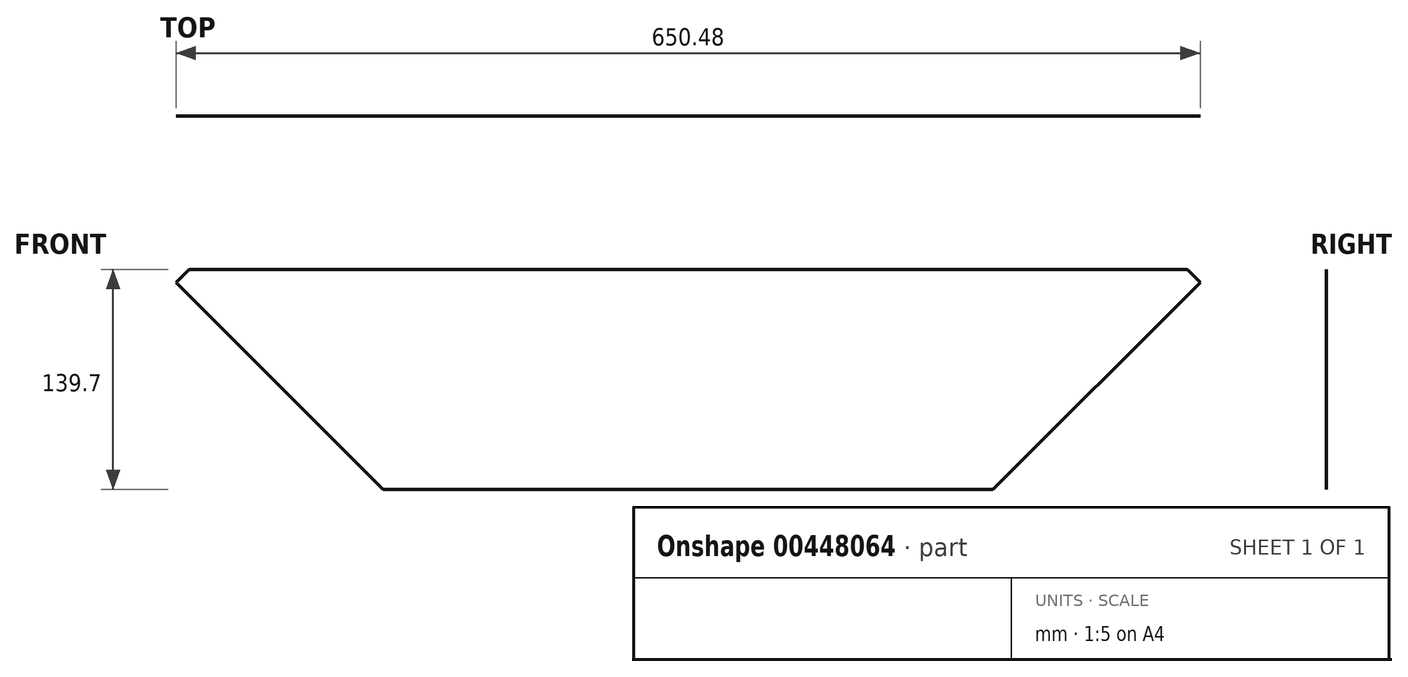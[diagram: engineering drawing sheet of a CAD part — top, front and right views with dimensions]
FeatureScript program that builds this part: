
annotation { "Feature Type Name" : "Feature", "Feature Type Description" : "" }
export const myFeature = defineFeature(function(context is Context, id is Id, definition is map)
    precondition{}
    {
        {
            var Q0;
            Q0=qCreatedBy(makeId("Front.planeOp"),FACE);
            var sketch = newSketch(context, id + "F0", { "sketchPlane" : qUnion([Q0])});
            skLineSegment(sketch, "E0", {"start": v(0, 0) * mm, "end": v(193.68, 0) * mm});
            skLineSegment(sketch, "E1", {"start": v(0, 0) * mm, "end": v(0, 139.7) * mm});
            skLineSegment(sketch, "E2", {"start": v(0, 139.7) * mm, "end": v(333.38, 139.7) * mm});
            skLineSegment(sketch, "E3", {"start": v(193.68, 0) * mm, "end": v(333.38, 139.7) * mm});
            skLineSegment(sketch, "E4.MirrorCS", {"start": v(0, 139.7) * mm, "end": v(-333.38, 139.7) * mm});
            skLineSegment(sketch, "E5.MirrorCS", {"start": v(0, 0) * mm, "end": v(-193.68, 0) * mm});
            skLineSegment(sketch, "E6.MirrorCS", {"start": v(-193.67, 0) * mm, "end": v(-333.37, 139.7) * mm});
            skLineSegment(sketch, "E7", {"start": v(-325.24, 131.56) * mm, "end": v(-317.1, 139.7) * mm});
            skLineSegment(sketch, "E8.MirrorCS", {"start": v(325.24, 131.56) * mm, "end": v(317.1, 139.7) * mm});
            skSolve(sketch);
        }
        {
            var Q0;
            Q0=makeQuery(id+"F0.imprint","IMPRINT",FACE,{"disambiguationData":[TD([[makeQuery(id+"F0.imprint","IMPRINT",EDGE,{"derivedFrom":sQuery(id+"F0.wireOp",EDGE,"E1")}),1.0]])]});
            var Q1;
            Q1=makeQuery(id+"F0.imprint","IMPRINT",FACE,{"disambiguationData":[TD([[makeQuery(id+"F0.imprint","IMPRINT",EDGE,{"derivedFrom":sQuery(id+"F0.wireOp",EDGE,"E0")}),1.0]])]});
            extrude(context, id + "F1", {"entities" : qUnion([Q0, Q1]), "depth" : 1 / 203.2 * mm});
        }
    });
